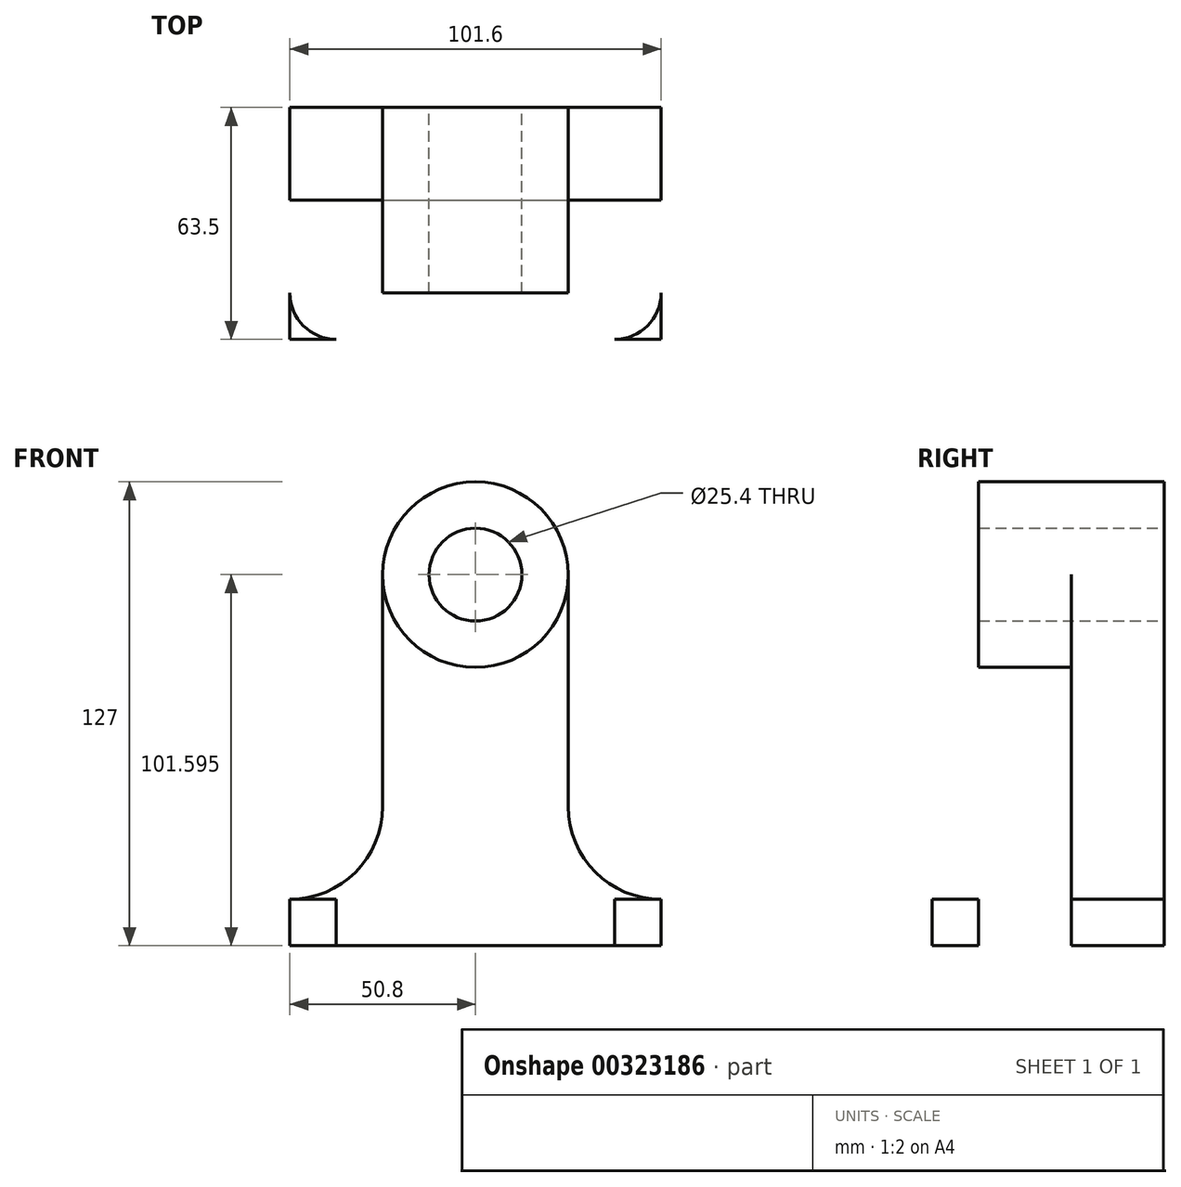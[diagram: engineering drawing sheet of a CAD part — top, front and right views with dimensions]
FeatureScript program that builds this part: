
annotation { "Feature Type Name" : "Feature", "Feature Type Description" : "" }
export const myFeature = defineFeature(function(context is Context, id is Id, definition is map)
    precondition{}
    {
        {
            var Q0;
            Q0=qCreatedBy(makeId("Front.planeOp"),FACE);
            var sketch = newSketch(context, id + "F0", { "sketchPlane" : qUnion([Q0])});
            skCircle(sketch, "E0", {"center": v(0, 40.53) * mm, "radius": 12.7 * mm});
            skLineSegment(sketch, "E1", {"start": v(-25.4, 40.53) * mm, "end": v(-25.4, -22.97) * mm});
            skLineSegment(sketch, "E2", {"start": v(25.4, 40.53) * mm, "end": v(25.4, -22.97) * mm});
            skArc(sketch, "E3", {"start": v(-25.4, -22.97) * mm, "mid": v(-32.84, -40.94) * mm, "end": v(-50.8, -48.37) * mm});
            skArc(sketch, "E4", {"start": v(25.4, -22.97) * mm, "mid": v(32.84, -40.94) * mm, "end": v(50.8, -48.37) * mm});
            skLineSegment(sketch, "E5.bottom", {"start": v(-50.8, -48.37) * mm, "end": v(50.8, -48.37) * mm});
            skLineSegment(sketch, "E5.top", {"start": v(-50.8, -61.07) * mm, "end": v(50.8, -61.07) * mm});
            skLineSegment(sketch, "E5.left", {"start": v(-50.8, -48.37) * mm, "end": v(-50.8, -61.07) * mm});
            skLineSegment(sketch, "E5.right", {"start": v(50.8, -48.37) * mm, "end": v(50.8, -61.07) * mm});
            skCircle(sketch, "E6", {"center": v(0, 40.53) * mm, "radius": 25.4 * mm});
            skSolve(sketch);
        }
        {
            var Q0;
            {var subQ1=sQuery(id+"F0.wireOp",EDGE,"E1");Q0=makeQuery(id+"F0.imprint","IMPRINT",FACE,{"disambiguationData":[TD([[makeQuery(id+"F0.imprint","IMPRINT",EDGE,{"derivedFrom":subQ1}),1.0]])]});}
            extrude(context, id + "F1", {"entities" : qUnion([Q0]), "depth" : 25.4 * mm});
        }
        {
            var Q0;
            Q0=makeQuery(id+"F0.imprint","IMPRINT",FACE,{"disambiguationData":[TD([[makeQuery(id+"F0.imprint","IMPRINT",EDGE,{"derivedFrom":sQuery(id+"F0.wireOp",EDGE,"E0")}),-1.0]])]});
            extrude(context, id + "F2", {"entities" : qUnion([Q0]), "operationType" : NewBodyOperationType.ADD, "depth" : 50.8 * mm});
        }
        {
            var Q0;
            Q0=makeQuery(id+"F0.imprint","IMPRINT",FACE,{"disambiguationData":[TD([[makeQuery(id+"F0.imprint","IMPRINT",EDGE,{"derivedFrom":sQuery(id+"F0.wireOp",EDGE,"E5.bottom")}),-1.0]])]});
            extrude(context, id + "F3", {"entities" : qUnion([Q0]), "operationType" : NewBodyOperationType.ADD, "depth" : 63.5 * mm});
        }
        {
            var Q0;
            Q0=makeQuery(id+"F3.opExtrude","SWEPT_FACE",FACE,{"disambiguationData":[OSD([sQuery(id+"F0.wireOp",EDGE,"E5.bottom")])]});
            var sketch = newSketch(context, id + "F4", { "sketchPlane" : qUnion([Q0])});
            skArc(sketch, "E7", {"start": v(-38.1, -63.5) * mm, "mid": v(-47.08, -59.78) * mm, "end": v(-50.8, -50.8) * mm});
            skArc(sketch, "E8", {"start": v(50.8, -50.8) * mm, "mid": v(47.08, -59.78) * mm, "end": v(38.1, -63.5) * mm});
            skCircle(sketch, "E9", {"center": v(-31.75, -44.45) * mm, "radius": 6.35 * mm});
            skCircle(sketch, "E10", {"center": v(31.75, -44.45) * mm, "radius": 6.35 * mm});
            skSolve(sketch);
        }
        {
            var Q0;
            Q0=makeQuery(id+"F4.imprint","IMPRINT",FACE,{"disambiguationData":[TD([[makeQuery(id+"F4.imprint","IMPRINT",EDGE,{"derivedFrom":sQuery(id+"F4.wireOp",EDGE,"E9")}),1.0]])]});
            var Q1;
            {var subQ0=sQuery(id+"F4.wireOp",EDGE,"E7");Q1=makeQuery(id+"F4.imprint","IMPRINT",FACE,{"disambiguationData":[TD([[makeQuery(id+"F4.imprint","IMPRINT",EDGE,{"derivedFrom":subQ0}),1.0]])]});}
            var Q2;
            {var subQ0=sQuery(id+"F4.wireOp",EDGE,"E8");Q2=makeQuery(id+"F4.imprint","IMPRINT",FACE,{"disambiguationData":[TD([[makeQuery(id+"F4.imprint","IMPRINT",EDGE,{"derivedFrom":subQ0}),1.0]])]});}
            var Q3;
            Q3=makeQuery(id+"F4.imprint","IMPRINT",FACE,{"disambiguationData":[TD([[makeQuery(id+"F4.imprint","IMPRINT",EDGE,{"derivedFrom":sQuery(id+"F4.wireOp",EDGE,"E10")}),1.0]])]});
            extrude(context, id + "F5", {"entities" : qUnion([Q0, Q1, Q2, Q3]), "operationType" : NewBodyOperationType.REMOVE, "oppositeDirection" : true, "depth" : 12.7 * mm});
        }
    });
